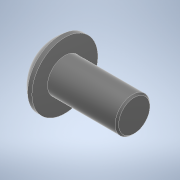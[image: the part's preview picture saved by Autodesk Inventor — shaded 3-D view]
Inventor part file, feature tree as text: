
AUTODESK INVENTOR PART (.ipt)
format: ipt  version: 2022 (Build 260153000, 153)  size: 140,800 bytes
history: native  units: mm
features: sketch x2, revolve x1, extrude x1, chamfer x1
ambient origin geometry x8: Origin, YZ Plane, XZ Plane, XY Plane, X Axis, Y Axis, Z Axis, Center Point
bodies: Solid1 (feature_tree)
feature tree (5):
  revolve  "Revolution1"  [1 undecoded]
  extrude  "Extrusion1"  Depth=2.0mm
  chamfer  "Chamfer1"  Distance=2.0mm
  sketch  "Sketch1"  dims[d0=2.2mm d1=8.0mm]
  sketch  "Sketch2"  dims[d2=3.8mm d4=0.5mm d5=2.0mm d6=90.0deg d7=1.5mm d8=2.5mm d9=1.3mm d10=0.0mm d11=0.2mm d12=2.0mm d13=45.0deg]
note: 1 required parameter value undecoded (feature->parameter linkage not recoverable at this tier; creation-order binding heuristic only, values carry confidence <= 0.55)
